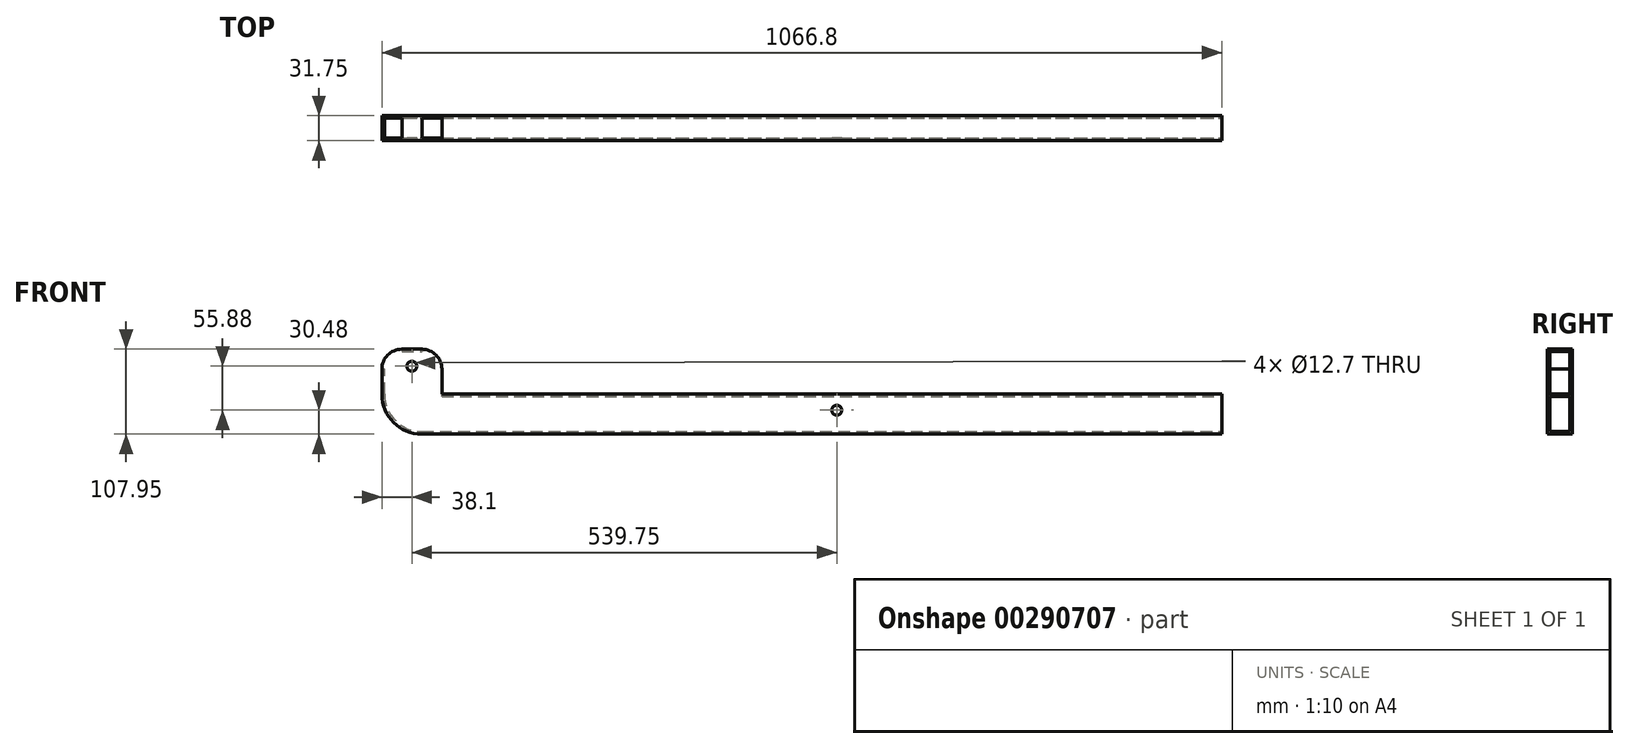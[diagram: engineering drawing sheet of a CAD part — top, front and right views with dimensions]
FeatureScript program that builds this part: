
annotation { "Feature Type Name" : "Feature", "Feature Type Description" : "" }
export const myFeature = defineFeature(function(context is Context, id is Id, definition is map)
    precondition{}
    {
        {
            var Q0;
            Q0=qCreatedBy(makeId("Front.planeOp"),FACE);
            var sketch = newSketch(context, id + "F0", { "sketchPlane" : qUnion([Q0])});
            skLineSegment(sketch, "E0.bottom", {"start": v(76.2, 0) * mm, "end": v(1066.8, 0) * mm});
            skLineSegment(sketch, "E0.top", {"start": v(50.8, -50.8) * mm, "end": v(1066.8, -50.8) * mm});
            skLineSegment(sketch, "E0.left", {"start": v(0, 0) * mm, "end": v(0, 0) * mm});
            skLineSegment(sketch, "E0.right", {"start": v(1066.8, 0) * mm, "end": v(1066.8, -50.8) * mm});
            skLineSegment(sketch, "E1.top", {"start": v(25.4, 57.15) * mm, "end": v(50.8, 57.15) * mm});
            skLineSegment(sketch, "E1.left", {"start": v(0, 0) * mm, "end": v(0, 31.75) * mm});
            skLineSegment(sketch, "E1.right", {"start": v(76.2, 0) * mm, "end": v(76.2, 31.75) * mm});
            skPoint(sketch, "E2.visualSharp", {"position": v(0, 57.15) * mm});
            skArc(sketch, "E2.filletArc", {"start": v(25.4, 57.15) * mm, "mid": v(7.44, 49.71) * mm, "end": v(0, 31.75) * mm});
            skPoint(sketch, "E3.visualSharp", {"position": v(76.2, 57.15) * mm});
            skArc(sketch, "E3.filletArc", {"start": v(76.2, 31.75) * mm, "mid": v(68.76, 49.71) * mm, "end": v(50.8, 57.15) * mm});
            skCircle(sketch, "E4", {"center": v(38.1, 35.56) * mm, "radius": 6.35 * mm});
            skPoint(sketch, "E5", {"position": v(38.1, 57.15) * mm});
            skPoint(sketch, "E6.visualSharp", {"position": v(0, -50.8) * mm});
            skArc(sketch, "E6.filletArc", {"start": v(0, 0) * mm, "mid": v(14.88, -35.92) * mm, "end": v(50.8, -50.8) * mm});
            skCircle(sketch, "E7", {"center": v(577.85, -20.32) * mm, "radius": 6.35 * mm});
            skSolve(sketch);
        }
        {
            var Q0;
            Q0=makeQuery(id+"F0.imprint","IMPRINT",FACE,{"disambiguationData":[TD([[makeQuery(id+"F0.imprint","IMPRINT",EDGE,{"derivedFrom":sQuery(id+"F0.wireOp",EDGE,"E0.bottom")}),-1.0]])]});
            extrude(context, id + "F1", {"entities" : qUnion([Q0]), "depth" : 31.75 * mm});
        }
        {
            var Q0;
            Q0=makeQuery(id+"F1.opExtrude","SWEPT_FACE",FACE,{"disambiguationData":[OSD([sQuery(id+"F0.wireOp",EDGE,"E2.filletArc")])]});
            var Q1;
            Q1=makeQuery(id+"F1.opExtrude","SWEPT_FACE",FACE,{"disambiguationData":[OSD([sQuery(id+"F0.wireOp",EDGE,"E4")])]});
            var Q2;
            Q2=makeQuery(id+"F1.opExtrude","SWEPT_FACE",FACE,{"disambiguationData":[OSD([sQuery(id+"F0.wireOp",EDGE,"E3.filletArc")])]});
            var Q3;
            Q3=makeQuery(id+"F1.opExtrude","SWEPT_FACE",FACE,{"disambiguationData":[OSD([sQuery(id+"F0.wireOp",EDGE,"E1.right")])]});
            var Q4;
            Q4=makeQuery(id+"F1.opExtrude","SWEPT_FACE",FACE,{"disambiguationData":[OSD([sQuery(id+"F0.wireOp",EDGE,"E0.right")])]});
            var Q5;
            Q5=makeQuery(id+"F1.opExtrude","SWEPT_FACE",FACE,{"disambiguationData":[OSD([sQuery(id+"F0.wireOp",EDGE,"E7")])]});
            shell(context, id + "F2", {"entities" : qUnion([Q0, Q1, Q2, Q3, Q4, Q5]), "thickness" : 3.17 * mm});
        }
    });
